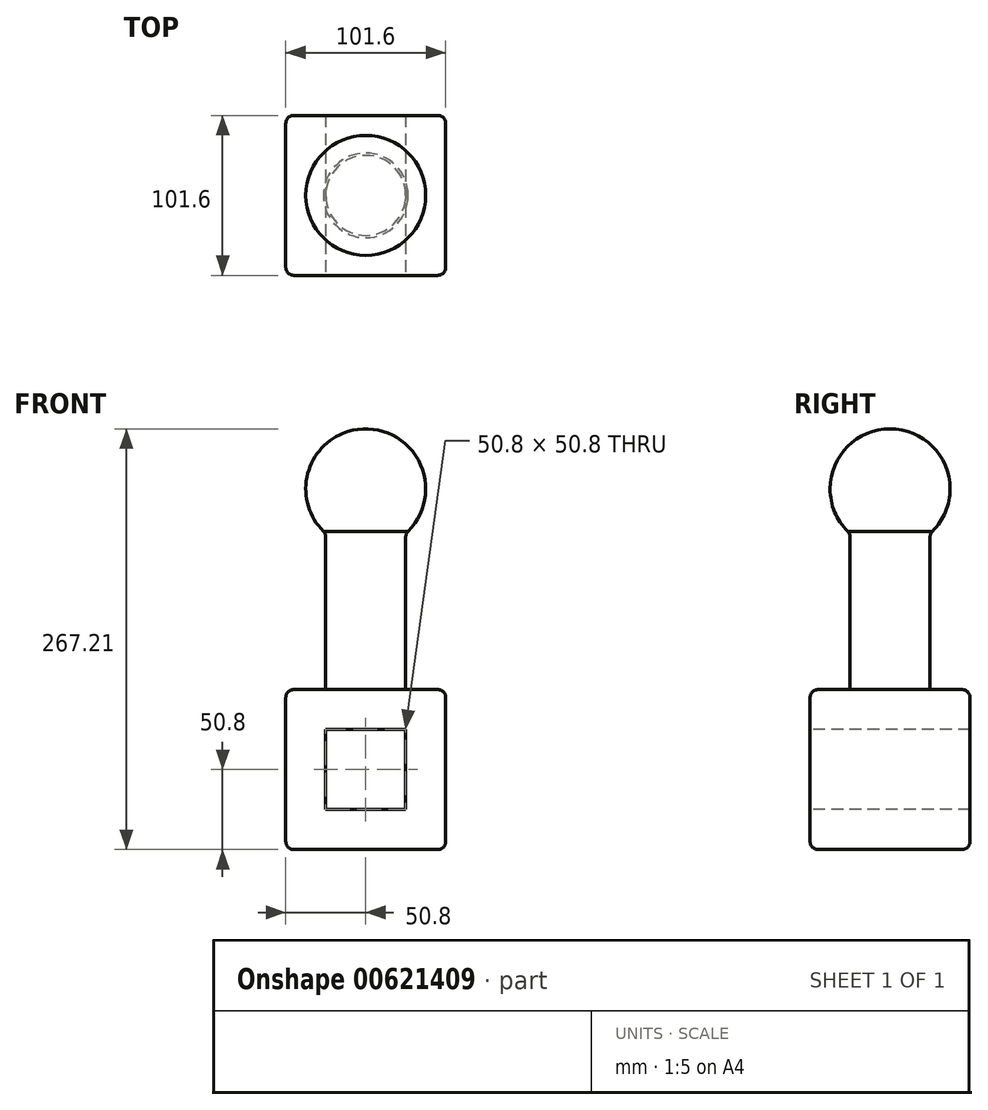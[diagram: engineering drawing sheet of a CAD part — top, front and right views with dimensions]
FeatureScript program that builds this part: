
annotation { "Feature Type Name" : "Feature", "Feature Type Description" : "" }
export const myFeature = defineFeature(function(context is Context, id is Id, definition is map)
    precondition{}
    {
        {
            var Q0;
            Q0=qCreatedBy(makeId("Top.planeOp"),FACE);
            var sketch = newSketch(context, id + "F0", { "sketchPlane" : qUnion([Q0])});
            skLineSegment(sketch, "E0.bottom", {"start": v(50.8, -50.8) * mm, "end": v(-50.8, -50.8) * mm});
            skLineSegment(sketch, "E0.top", {"start": v(50.8, 50.8) * mm, "end": v(-50.8, 50.8) * mm});
            skLineSegment(sketch, "E0.left", {"start": v(50.8, -50.8) * mm, "end": v(50.8, 50.8) * mm});
            skLineSegment(sketch, "E0.right", {"start": v(-50.8, -50.8) * mm, "end": v(-50.8, 50.8) * mm});
            skPoint(sketch, "E0.middle", {"position": v(0, 0) * mm});
            skSolve(sketch);
        }
        {
            var Q0;
            Q0=qSketchRegion(id+"F0",true);
            extrude(context, id + "F1", {"entities" : qUnion([Q0]), "depth" : 101.6 * mm, "offsetDistance" : 25.4 * mm});
        }
        {
            var Q0;
            Q0=makeQuery(id+"F1.opExtrude","CAP_FACE",FACE,{"disambiguationData":[OSD([sQuery(id+"F0.wireOp",EDGE,"E0.bottom"),sQuery(id+"F0.wireOp",EDGE,"E0.top"),sQuery(id+"F0.wireOp",EDGE,"E0.left"),sQuery(id+"F0.wireOp",EDGE,"E0.right")])],"isStart":false});
            var sketch = newSketch(context, id + "F2", { "sketchPlane" : qUnion([Q0])});
            skCircle(sketch, "E1", {"center": v(0, 0) * mm, "radius": 25.4 * mm});
            skSolve(sketch);
        }
        {
            var Q0;
            Q0=qSketchRegion(id+"F2",true);
            extrude(context, id + "F3", {"entities" : qUnion([Q0]), "operationType" : NewBodyOperationType.ADD, "depth" : 127.5 * mm, "offsetDistance" : 25.4 * mm});
        }
        {
            var Q0;
            Q0=makeQuery(id+"F3.opExtrude","CAP_FACE",FACE,{"disambiguationData":[OSD([sQuery(id+"F2.wireOp",EDGE,"E1")])],"isStart":false});
            var sketch = newSketch(context, id + "F4", { "sketchPlane" : qUnion([Q0])});
            skArc(sketch, "E2", {"start": v(0, -38.1) * mm, "mid": v(38.1, 0) * mm, "end": v(0, 38.1) * mm});
            skLineSegment(sketch, "E3", {"start": v(0, 38.1) * mm, "end": v(0, -38.1) * mm});
            skSolve(sketch);
        }
        {
            var Q0;
            {var subQ0=sQuery(id+"F4.wireOp",EDGE,"E2");Q0=makeQuery(id+"F4.imprint","IMPRINT",FACE,{"disambiguationData":[TD([[makeQuery(id+"F4.imprint","IMPRINT",EDGE,{"derivedFrom":subQ0}),1.0]])]});}
            var Q1;
            {var subQ0=sQuery(id+"F4.wireOp",EDGE,"E3");var subQ1=makeQuery(id+"F3.opExtrude","CAP_EDGE",EDGE,{"disambiguationData":[OSD([sQuery(id+"F2.wireOp",EDGE,"E1")])],"isStart":false});var subQ2=makeQuery(id+"F4.imprint","INTERSECT",VERTEX,{"disambiguationData":[OD(0.0)],"derivedFrom":[subQ1,subQ0]});Q1=makeQuery(id+"F4.imprint","IMPRINT",FACE,{"disambiguationData":[TD([[makeQuery(id+"F4.imprint","IMPRINT",EDGE,{"disambiguationData":[TD([[subQ2,-1.0]])],"derivedFrom":subQ0}),-1.0]])]});}
            var Q2;
            Q2=sQuery(id+"F4.wireOp",EDGE,"E3");
            revolve(context, id + "F5", {"operationType" : NewBodyOperationType.ADD, "entities" : qUnion([Q0, Q1]), "axis" : qUnion([Q2]), "revolveType" : RevolveType.FULL});
        }
        {
            var Q0;
            Q0=makeQuery(id+"F1.opExtrude","SWEPT_FACE",FACE,{"disambiguationData":[OSD([sQuery(id+"F0.wireOp",EDGE,"E0.bottom")])]});
            var sketch = newSketch(context, id + "F6", { "sketchPlane" : qUnion([Q0])});
            skLineSegment(sketch, "E4.bottom", {"start": v(25.4, 25.4) * mm, "end": v(-25.4, 25.4) * mm});
            skLineSegment(sketch, "E4.top", {"start": v(25.4, 76.2) * mm, "end": v(-25.4, 76.2) * mm});
            skLineSegment(sketch, "E4.left", {"start": v(25.4, 25.4) * mm, "end": v(25.4, 76.2) * mm});
            skLineSegment(sketch, "E4.right", {"start": v(-25.4, 25.4) * mm, "end": v(-25.4, 76.2) * mm});
            skPoint(sketch, "E4.middle", {"position": v(0, 50.8) * mm});
            skSolve(sketch);
        }
        {
            var Q0;
            Q0=makeQuery(id+"F6.imprint","IMPRINT",FACE,{"disambiguationData":[TD([[makeQuery(id+"F6.imprint","IMPRINT",EDGE,{"derivedFrom":sQuery(id+"F6.wireOp",EDGE,"E4.bottom")}),-1.0]])]});
            extrude(context, id + "F7", {"entities" : qUnion([Q0]), "operationType" : NewBodyOperationType.REMOVE, "oppositeDirection" : true, "depth" : 101.6 * mm, "offsetDistance" : 25.4 * mm});
        }
        {
            var Q0;
            Q0=makeQuery(id+"F1.opExtrude","CAP_EDGE",EDGE,{"disambiguationData":[OSD([sQuery(id+"F0.wireOp",EDGE,"E0.bottom")])],"isStart":false});
            var Q1;
            Q1=makeQuery(id+"F1.opExtrude","CAP_EDGE",EDGE,{"disambiguationData":[OSD([sQuery(id+"F0.wireOp",EDGE,"E0.right")])],"isStart":false});
            var Q2;
            Q2=makeQuery(id+"F1.opExtrude","CAP_EDGE",EDGE,{"disambiguationData":[OSD([sQuery(id+"F0.wireOp",EDGE,"E0.left")])],"isStart":false});
            var Q3;
            Q3=makeQuery(id+"F1.opExtrude","CAP_EDGE",EDGE,{"disambiguationData":[OSD([sQuery(id+"F0.wireOp",EDGE,"E0.top")])],"isStart":false});
            var Q4;
            Q4=makeQuery(id+"F1.opExtrude","SWEPT_EDGE",EDGE,{"disambiguationData":[OSD([sQuery(id+"F0.wireOp",EDGE,"E0.bottom"),sQuery(id+"F0.wireOp",EDGE,"E0.left")])]});
            var Q5;
            Q5=makeQuery(id+"F1.opExtrude","SWEPT_EDGE",EDGE,{"disambiguationData":[OSD([sQuery(id+"F0.wireOp",EDGE,"E0.top"),sQuery(id+"F0.wireOp",EDGE,"E0.left")])]});
            var Q6;
            Q6=makeQuery(id+"F1.opExtrude","CAP_EDGE",EDGE,{"disambiguationData":[OSD([sQuery(id+"F0.wireOp",EDGE,"E0.left")])],"isStart":true});
            var Q7;
            Q7=makeQuery(id+"F1.opExtrude","CAP_EDGE",EDGE,{"disambiguationData":[OSD([sQuery(id+"F0.wireOp",EDGE,"E0.bottom")])],"isStart":true});
            var Q8;
            Q8=makeQuery(id+"F1.opExtrude","SWEPT_EDGE",EDGE,{"disambiguationData":[OSD([sQuery(id+"F0.wireOp",EDGE,"E0.bottom"),sQuery(id+"F0.wireOp",EDGE,"E0.right")])]});
            var Q9;
            Q9=makeQuery(id+"F1.opExtrude","SWEPT_FACE",FACE,{"disambiguationData":[OSD([sQuery(id+"F0.wireOp",EDGE,"E0.right")])]});
            var Q10;
            Q10=makeQuery(id+"F1.opExtrude","SWEPT_EDGE",EDGE,{"disambiguationData":[OSD([sQuery(id+"F0.wireOp",EDGE,"E0.top"),sQuery(id+"F0.wireOp",EDGE,"E0.right")])]});
            var Q11;
            Q11=makeQuery(id+"F1.opExtrude","CAP_EDGE",EDGE,{"disambiguationData":[OSD([sQuery(id+"F0.wireOp",EDGE,"E0.top")])],"isStart":true});
            var Q12;
            Q12=makeQuery(id+"F5.boolean.opBoolean","INTERSECT",EDGE,{"derivedFrom":[makeQuery(id+"F3.opExtrude","SWEPT_FACE",FACE,{"disambiguationData":[OSD([sQuery(id+"F2.wireOp",EDGE,"E1")])]}),makeQuery(id+"F5.opRevolve","SWEPT_FACE",FACE,{"disambiguationData":[OSD([sQuery(id+"F4.wireOp",EDGE,"E2")])]})]});
            var Q13;
            Q13=makeQuery(id+"F3.opExtrude","CAP_EDGE",EDGE,{"disambiguationData":[OSD([sQuery(id+"F2.wireOp",EDGE,"E1")])],"isStart":true});
            fillet(context, id + "F8", {"entities" : qUnion([Q0, Q1, Q2, Q3, Q4, Q5, Q6, Q7, Q8, Q9, Q10, Q11, Q12, Q13]), "radius" : 5.08 * mm, "tangentPropagation" : true, "allowEdgeOverflow" : false});
        }
    });
